# Revit family: 14-100-011_green_simplified
name_source: partatom
category: Generic Models
units: mm (PartAtom-declared; Revit-internal decimal feet)

## family parameters
Always vertical = Yes
Can host rebar = No
Cut with Voids When Loaded = No
Part Type = Normal
Room Calculation Point = No
Round Connector Dimension = Use Diameter
Shared = No
Work Plane-Based = No

## types (1)
- Type 1
    Artnr = 14-100-011
    Artnr_green_simplified = 14-101-011
    CheckedDate = -
    CheckedDate_green_simplified = -
    Default Elevation = 0 mm  [stored 0 ft]
    Description = Rauland
    Description_green_simplified = Rauland 2
    Number = 20445
    Number_green_simplified = 20445
    PartName = Rauland
    PartName_green_simplified = Rauland 2
    Revision = 0
    Revision_green_simplified = 0
    Weight = 30938.3

note: [stored X ft] marks values corroborated as IEEE doubles in the binary element streams (Revit-internal decimal feet)

## geometry (parser evidence)
native form markers: Sweep x28
no freeform markers — native parametric forms only
